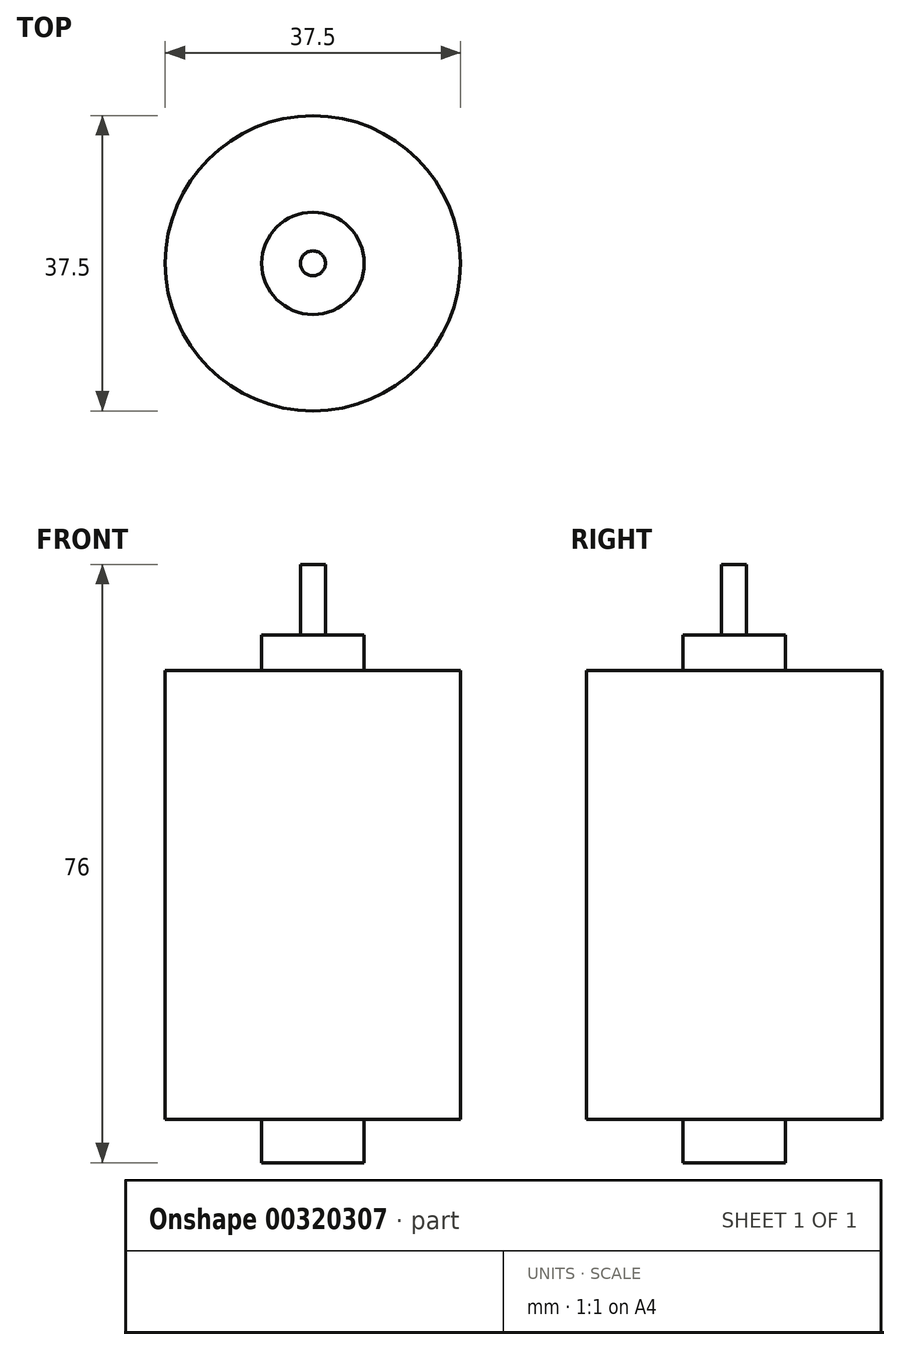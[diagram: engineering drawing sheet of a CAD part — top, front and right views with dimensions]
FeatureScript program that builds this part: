
annotation { "Feature Type Name" : "Feature", "Feature Type Description" : "" }
export const myFeature = defineFeature(function(context is Context, id is Id, definition is map)
    precondition{}
    {
        {
            var Q0;
            Q0=qCreatedBy(makeId("Top.planeOp"),FACE);
            var sketch = newSketch(context, id + "F0", { "sketchPlane" : qUnion([Q0])});
            skCircle(sketch, "E0", {"center": v(0, 0) * mm, "radius": 6.5 * mm});
            skCircle(sketch, "E1", {"center": v(0, 0) * mm, "radius": 18.75 * mm});
            skSolve(sketch);
        }
        {
            var Q0;
            Q0=makeQuery(id+"F0.imprint","IMPRINT",FACE,{"disambiguationData":[TD([[makeQuery(id+"F0.imprint","IMPRINT",EDGE,{"derivedFrom":sQuery(id+"F0.wireOp",EDGE,"E0")}),1.0]])]});
            extrude(context, id + "F1", {"entities" : qUnion([Q0]), "depth" : 33 * mm});
        }
        {
            var Q0;
            Q0 = qSketchRegion(id + "F0", true);
            extrude(context, id + "F2", {"entities" : qUnion([Q0]), "operationType" : NewBodyOperationType.ADD, "endBound" : BoundingType.SYMMETRIC, "depth" : 57 * mm});
        }
        {
            var Q0;
            Q0=qCreatedBy(makeId("Top.planeOp"),FACE);
            var sketch = newSketch(context, id + "F3", { "sketchPlane" : qUnion([Q0])});
            skCircle(sketch, "E2", {"center": v(0, 0) * mm, "radius": 6.5 * mm});
            skSolve(sketch);
        }
        {
            var Q0;
            Q0 = qSketchRegion(id + "F3", true);
            extrude(context, id + "F4", {"entities" : qUnion([Q0]), "operationType" : NewBodyOperationType.ADD, "oppositeDirection" : true, "depth" : 34 * mm});
        }
        {
            var Q0;
            Q0=qCreatedBy(makeId("Top.planeOp"),FACE);
            var sketch = newSketch(context, id + "F5", { "sketchPlane" : qUnion([Q0])});
            skCircle(sketch, "E3", {"center": v(0, 0) * mm, "radius": 1.59 * mm});
            skSolve(sketch);
        }
        {
            var Q0;
            Q0 = qSketchRegion(id + "F5", true);
            extrude(context, id + "F6", {"entities" : qUnion([Q0]), "operationType" : NewBodyOperationType.ADD, "depth" : 42 * mm});
        }
    });
